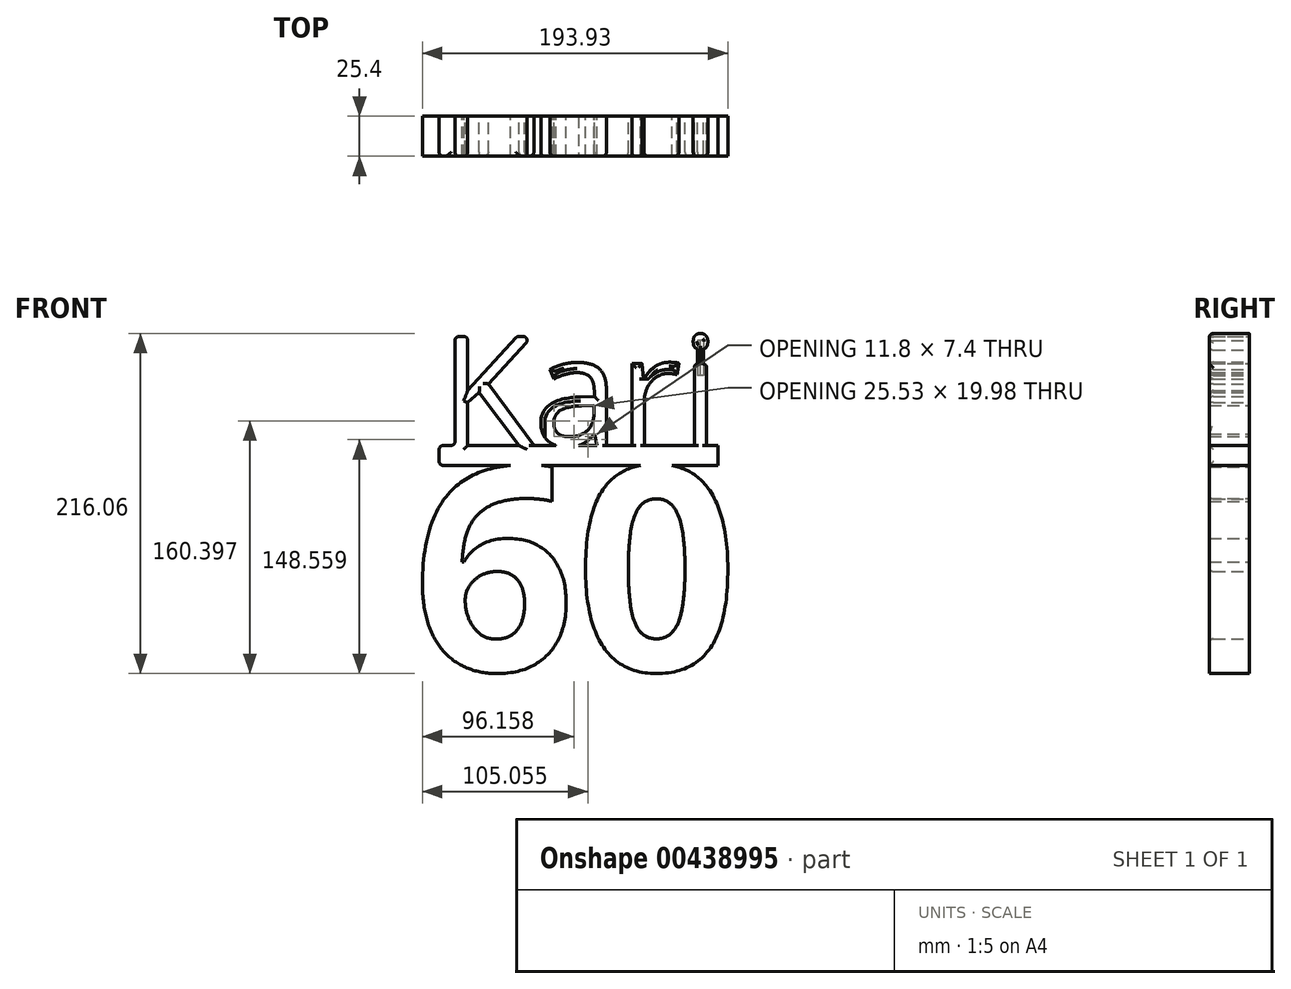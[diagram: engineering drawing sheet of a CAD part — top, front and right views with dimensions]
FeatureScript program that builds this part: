
annotation { "Feature Type Name" : "Feature", "Feature Type Description" : "" }
export const myFeature = defineFeature(function(context is Context, id is Id, definition is map)
    precondition{}
    {
        {
            var Q0;
            Q0=qCreatedBy(makeId("Front.planeOp"),FACE);
            var sketch = newSketch(context, id + "F0", { "sketchPlane" : qUnion([Q0])});
            skText(sketch, "E0", { "text": "60", "fontName": "OpenSans-Bold.ttf"});
            skLineSegment(sketch, "E1.bottom", {"start": v(-176.94, 0) * mm, "end": v(0, 0) * mm});
            skLineSegment(sketch, "E1.top", {"start": v(-176.94, 12.68) * mm, "end": v(0, 12.68) * mm});
            skLineSegment(sketch, "E1.left", {"start": v(-176.94, 0) * mm, "end": v(-176.94, 12.68) * mm});
            skLineSegment(sketch, "E1.right", {"start": v(0, 0) * mm, "end": v(0, 12.68) * mm});
            skText(sketch, "E2", { "text": "Kari", "fontName": "OpenSans-Regular.ttf"});
            const initialGuessF0  = {"E0": [-0.19388, -0.1304, 1, 0, 0.1304], "E2": [-0.17636, 0.01268, 1, 0, 0.06985]};
            skSetInitialGuess(sketch, initialGuessF0);
            skSolve(sketch);
        }
        {
            var Q0;
            Q0 = qSketchRegion(id + "F0", true);
            extrude(context, id + "F1", {"entities" : qUnion([Q0]), "endBound" : BoundingType.SYMMETRIC, "depth" : 25.4 * mm});
        }
        {
            var Q0;
            Q0=qCreatedBy(makeId("Front.planeOp"),FACE);
            var sketch = newSketch(context, id + "F2", { "sketchPlane" : qUnion([Q0])});
            skLineSegment(sketch, "E3.bottom", {"start": v(-9.05, 79.23) * mm, "end": v(-13.01, 79.23) * mm});
            skLineSegment(sketch, "E3.top", {"start": v(-9.05, 57.12) * mm, "end": v(-13.01, 57.12) * mm});
            skLineSegment(sketch, "E3.left", {"start": v(-9.05, 79.23) * mm, "end": v(-9.05, 57.12) * mm});
            skLineSegment(sketch, "E3.right", {"start": v(-13.01, 79.23) * mm, "end": v(-13.01, 57.12) * mm});
            skSolve(sketch);
        }
        {
            var Q0;
            Q0=makeQuery(id+"F2.imprint","IMPRINT",FACE,{"disambiguationData":[TD([[makeQuery(id+"F2.imprint","IMPRINT",EDGE,{"derivedFrom":sQuery(id+"F2.wireOp",EDGE,"E3.bottom")}),1.0]])]});
            extrude(context, id + "F3", {"entities" : qUnion([Q0]), "endBound" : BoundingType.SYMMETRIC, "depth" : 25.4 * mm});
        }
        {
            var Q0;
            Q0=makeQuery(id+"F1.opExtrude","CAP_EDGE",EDGE,{"disambiguationData":[OSD([sQuery(id+"F0.wireOp",EDGE,"E2.sketch_text.stroke-5")])],"isStart":false});
            var Q1;
            Q1=makeQuery(id+"F1.opExtrude","CAP_EDGE",EDGE,{"disambiguationData":[OSD([sQuery(id+"F0.wireOp",EDGE,"E2.sketch_text.stroke-6")])],"isStart":false});
            var Q2;
            Q2=makeQuery(id+"F1.opExtrude","CAP_EDGE",EDGE,{"disambiguationData":[OSD([sQuery(id+"F0.wireOp",EDGE,"E2.sketch_text.stroke-7")])],"isStart":false});
            var Q3;
            Q3=makeQuery(id+"F1.opExtrude","CAP_EDGE",EDGE,{"disambiguationData":[OSD([sQuery(id+"F0.wireOp",EDGE,"E2.sketch_text.stroke-8")])],"isStart":false});
            var Q4;
            Q4=makeQuery(id+"F1.opExtrude","CAP_EDGE",EDGE,{"disambiguationData":[OSD([sQuery(id+"F0.wireOp",EDGE,"E2.sketch_text.stroke-10")])],"isStart":false});
            var Q5;
            Q5=makeQuery(id+"F1.opExtrude","CAP_EDGE",EDGE,{"disambiguationData":[OSD([sQuery(id+"F0.wireOp",EDGE,"E2.sketch_text.stroke-11")])],"isStart":false});
            var Q6;
            Q6=makeQuery(id+"F1.opExtrude","CAP_EDGE",EDGE,{"disambiguationData":[OSD([sQuery(id+"F0.wireOp",EDGE,"E2.sketch_text.stroke-1")])],"isStart":false});
            var Q7;
            Q7=makeQuery(id+"F1.opExtrude","CAP_EDGE",EDGE,{"disambiguationData":[OSD([sQuery(id+"F0.wireOp",EDGE,"E2.sketch_text.stroke-2")])],"isStart":false});
            var Q8;
            Q8=makeQuery(id+"F1.opExtrude","CAP_EDGE",EDGE,{"disambiguationData":[OSD([sQuery(id+"F0.wireOp",EDGE,"E2.sketch_text.stroke-3")])],"isStart":false});
            var Q9;
            Q9=makeQuery(id+"F1.opExtrude","CAP_EDGE",EDGE,{"disambiguationData":[OSD([sQuery(id+"F0.wireOp",EDGE,"E2.sketch_text.stroke-23")])],"isStart":false});
            var Q10;
            Q10=makeQuery(id+"F1.opExtrude","CAP_EDGE",EDGE,{"disambiguationData":[OSD([sQuery(id+"F0.wireOp",EDGE,"E2.sketch_text.stroke-25")])],"isStart":false});
            var Q11;
            Q11=makeQuery(id+"F1.opExtrude","CAP_EDGE",EDGE,{"disambiguationData":[OSD([sQuery(id+"F0.wireOp",EDGE,"E2.sketch_text.stroke-24")])],"isStart":false});
            var Q12;
            Q12=makeQuery(id+"F1.opExtrude","CAP_EDGE",EDGE,{"disambiguationData":[OSD([sQuery(id+"F0.wireOp",EDGE,"E2.sketch_text.stroke-19")])],"isStart":false});
            var Q13;
            Q13=makeQuery(id+"F1.opExtrude","CAP_EDGE",EDGE,{"disambiguationData":[OSD([sQuery(id+"F0.wireOp",EDGE,"E2.sketch_text.stroke-46")])],"isStart":false});
            var Q14;
            Q14=makeQuery(id+"F1.opExtrude","CAP_EDGE",EDGE,{"disambiguationData":[OSD([sQuery(id+"F0.wireOp",EDGE,"E2.sketch_text.stroke-44")])],"isStart":false});
            var Q15;
            Q15=makeQuery(id+"F1.opExtrude","CAP_EDGE",EDGE,{"disambiguationData":[OSD([sQuery(id+"F0.wireOp",EDGE,"E2.sketch_text.stroke-51")])],"isStart":false});
            var Q16;
            Q16=makeQuery(id+"F1.opExtrude","CAP_EDGE",EDGE,{"disambiguationData":[OSD([sQuery(id+"F0.wireOp",EDGE,"E2.sketch_text.stroke-48")])],"isStart":false});
            var Q17;
            Q17=makeQuery(id+"F1.opExtrude","CAP_EDGE",EDGE,{"disambiguationData":[OSD([sQuery(id+"F0.wireOp",EDGE,"E2.sketch_text.stroke-47")])],"isStart":false});
            var Q18;
            Q18=makeQuery(id+"F1.opExtrude","CAP_EDGE",EDGE,{"disambiguationData":[OSD([sQuery(id+"F0.wireOp",EDGE,"E2.sketch_text.stroke-40")])],"isStart":false});
            var Q19;
            Q19=makeQuery(id+"F1.opExtrude","SWEPT_EDGE",EDGE,{"disambiguationData":[OSD([sQuery(id+"F0.wireOp",EDGE,"E2.sketch_text.stroke-5"),sQuery(id+"F0.wireOp",EDGE,"E2.sketch_text.stroke-6")])]});
            var Q20;
            Q20=makeQuery(id+"F1.opExtrude","SWEPT_EDGE",EDGE,{"disambiguationData":[OSD([sQuery(id+"F0.wireOp",EDGE,"E2.sketch_text.stroke-6"),sQuery(id+"F0.wireOp",EDGE,"E2.sketch_text.stroke-7")])]});
            var Q21;
            Q21=makeQuery(id+"F1.opExtrude","SWEPT_EDGE",EDGE,{"disambiguationData":[OSD([sQuery(id+"F0.wireOp",EDGE,"E2.sketch_text.stroke-9"),sQuery(id+"F0.wireOp",EDGE,"E2.sketch_text.stroke-10")])]});
            var Q22;
            Q22=makeQuery(id+"F1.opExtrude","SWEPT_EDGE",EDGE,{"disambiguationData":[OSD([sQuery(id+"F0.wireOp",EDGE,"E2.sketch_text.stroke-8"),sQuery(id+"F0.wireOp",EDGE,"E2.sketch_text.stroke-9")])]});
            var Q23;
            Q23=makeQuery(id+"F1.opExtrude","SWEPT_EDGE",EDGE,{"disambiguationData":[OSD([sQuery(id+"F0.wireOp",EDGE,"E1.top"),sQuery(id+"F0.wireOp",EDGE,"E2.sketch_text.stroke-4"),sQuery(id+"F0.wireOp",EDGE,"E2.sketch_text.stroke-5")])]});
            var Q24;
            Q24=makeQuery(id+"F1.opExtrude","SWEPT_EDGE",EDGE,{"disambiguationData":[OSD([sQuery(id+"F0.wireOp",EDGE,"E1.top"),sQuery(id+"F0.wireOp",EDGE,"E1.left")])]});
            var Q25;
            Q25=makeQuery(id+"F1.opExtrude","CAP_EDGE",EDGE,{"disambiguationData":[OSD([sQuery(id+"F0.wireOp",EDGE,"E1.left")])],"isStart":false});
            var Q26;
            Q26=makeQuery(id+"F1.opExtrude","SWEPT_EDGE",EDGE,{"disambiguationData":[OSD([sQuery(id+"F0.wireOp",EDGE,"E1.bottom"),sQuery(id+"F0.wireOp",EDGE,"E1.left")])]});
            var Q27;
            {var subQ0=sQuery(id+"F0.wireOp",EDGE,"E1.top");Q27=makeQuery(id+"F1.opExtrude","CAP_EDGE",EDGE,{"disambiguationData":[OSD([subQ0]),TDD([makeQuery(id+"F0.imprint","IMPRINT",EDGE,{"disambiguationData":[TD([[makeQuery(id+"F0.imprint","INTERSECT",VERTEX,{"derivedFrom":[subQ0,sQuery(id+"F0.wireOp",EDGE,"E2.sketch_text.stroke-0"),sQuery(id+"F0.wireOp",EDGE,"E2.sketch_text.stroke-1")]}),1.0]])],"derivedFrom":subQ0})])],"isStart":false});}
            var Q28;
            Q28=makeQuery(id+"F1.opExtrude","CAP_EDGE",EDGE,{"disambiguationData":[OSD([sQuery(id+"F0.wireOp",EDGE,"E2.sketch_text.stroke-53")])],"isStart":false});
            var Q29;
            Q29=makeQuery(id+"F1.opExtrude","CAP_EDGE",EDGE,{"disambiguationData":[OSD([sQuery(id+"F0.wireOp",EDGE,"E2.sketch_text.stroke-55")])],"isStart":false});
            var Q30;
            Q30=makeQuery(id+"F1.opExtrude","CAP_EDGE",EDGE,{"disambiguationData":[OSD([sQuery(id+"F0.wireOp",EDGE,"E2.sketch_text.stroke-57")])],"isStart":false});
            var Q31;
            Q31=makeQuery(id+"F3.opExtrude","CAP_EDGE",EDGE,{"disambiguationData":[OSD([sQuery(id+"F2.wireOp",EDGE,"E3.right")])],"isStart":false});
            var Q32;
            Q32=makeQuery(id+"F3.opExtrude","CAP_EDGE",EDGE,{"disambiguationData":[OSD([sQuery(id+"F2.wireOp",EDGE,"E3.left")])],"isStart":false});
            var Q33;
            Q33=makeQuery(id+"F1.opExtrude","SWEPT_EDGE",EDGE,{"disambiguationData":[OSD([sQuery(id+"F0.wireOp",EDGE,"E2.sketch_text.stroke-53"),sQuery(id+"F0.wireOp",EDGE,"E2.sketch_text.stroke-54")])]});
            var Q34;
            Q34=makeQuery(id+"F1.opExtrude","SWEPT_EDGE",EDGE,{"disambiguationData":[OSD([sQuery(id+"F0.wireOp",EDGE,"E2.sketch_text.stroke-54"),sQuery(id+"F0.wireOp",EDGE,"E2.sketch_text.stroke-55")])]});
            var Q35;
            Q35=makeQuery(id+"F1.opExtrude","CAP_EDGE",EDGE,{"disambiguationData":[OSD([sQuery(id+"F0.wireOp",EDGE,"E0.sketch_text.stroke-19")])],"isStart":false});
            var Q36;
            Q36=makeQuery(id+"F1.opExtrude","CAP_EDGE",EDGE,{"disambiguationData":[OSD([sQuery(id+"F0.wireOp",EDGE,"E0.sketch_text.stroke-38")])],"isStart":false});
            fillet(context, id + "F4", {"entities" : qUnion([Q0, Q1, Q2, Q3, Q4, Q5, Q6, Q7, Q8, Q9, Q10, Q11, Q12, Q13, Q14, Q15, Q16, Q17, Q18, Q19, Q20, Q21, Q22, Q23, Q24, Q25, Q26, Q27, Q28, Q29, Q30, Q31, Q32, Q33, Q34, Q35, Q36]), "radius" : 2.54 * mm, "tangentPropagation" : true, "allowEdgeOverflow" : false});
        }
    });
